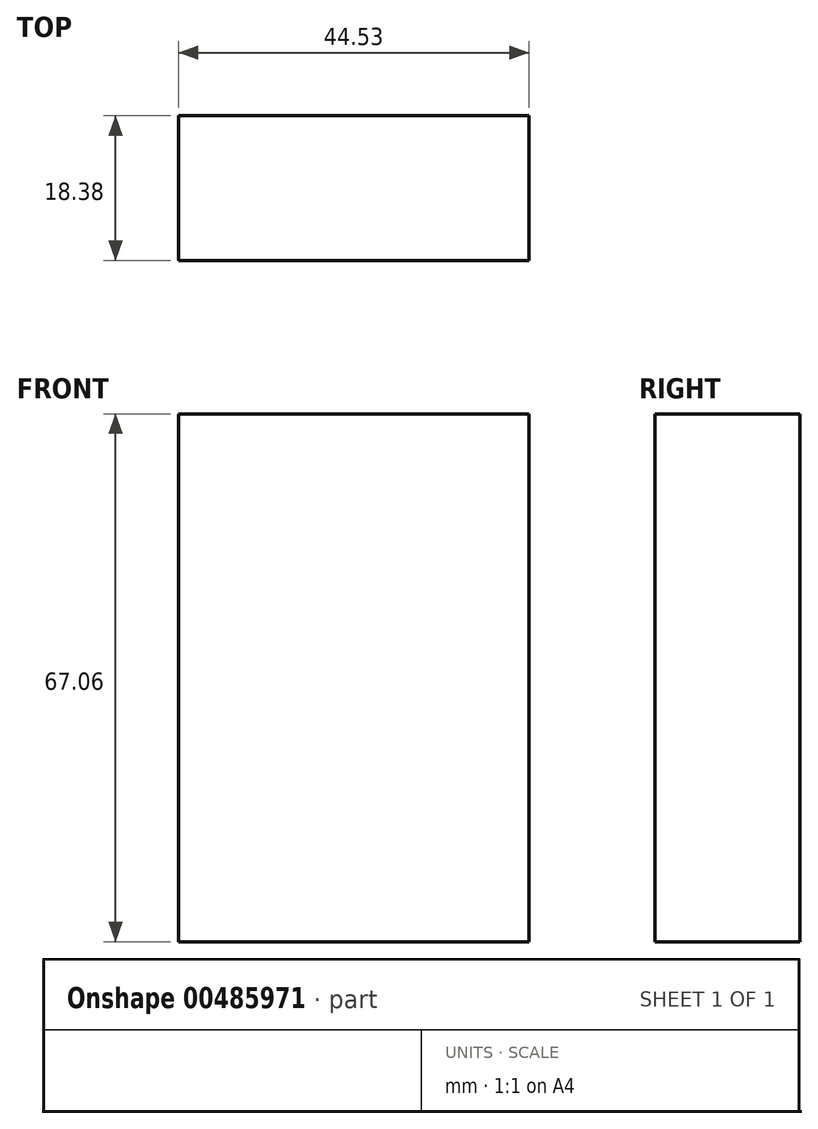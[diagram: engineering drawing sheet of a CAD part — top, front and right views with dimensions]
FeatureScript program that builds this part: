
annotation { "Feature Type Name" : "Feature", "Feature Type Description" : "" }
export const myFeature = defineFeature(function(context is Context, id is Id, definition is map)
    precondition{}
    {
        {
            var Q0;
            Q0=qCreatedBy(makeId("Top.planeOp"),FACE);
            var sketch = newSketch(context, id + "F0", { "sketchPlane" : qUnion([Q0])});
            skLineSegment(sketch, "E0.bottom", {"start": v(-100.35, 53.98) * mm, "end": v(-55.82, 53.98) * mm});
            skLineSegment(sketch, "E0.top", {"start": v(-100.35, 35.6) * mm, "end": v(-55.82, 35.6) * mm});
            skLineSegment(sketch, "E0.left", {"start": v(-100.35, 53.98) * mm, "end": v(-100.35, 35.6) * mm});
            skLineSegment(sketch, "E0.right", {"start": v(-55.82, 53.98) * mm, "end": v(-55.82, 35.6) * mm});
            skSolve(sketch);
        }
        {
            var Q0;
            Q0=makeQuery(id+"F0.imprint","IMPRINT",FACE,{"disambiguationData":[TD([[makeQuery(id+"F0.imprint","IMPRINT",EDGE,{"derivedFrom":sQuery(id+"F0.wireOp",EDGE,"E0.bottom")}),-1.0]])]});
            extrude(context, id + "F1", {"entities" : qUnion([Q0]), "depth" : 67.06 * mm});
        }
    });
